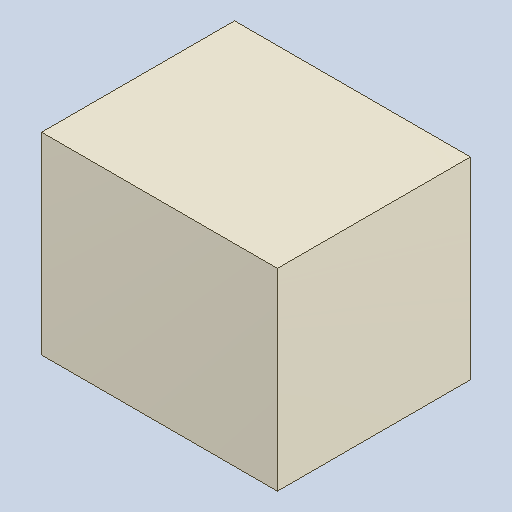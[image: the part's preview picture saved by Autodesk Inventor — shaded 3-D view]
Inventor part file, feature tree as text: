
AUTODESK INVENTOR PART (.ipt)
format: ipt  version: 2023.4 (Build 274418000, 418)  size: 81,920 bytes
history: native  units: mm
features: extrude x1
ambient origin geometry x8: Origin, YZ Plane, XZ Plane, XY Plane, X Axis, Y Axis, Z Axis, Center Point
bodies: Solid1 (feature_tree)
feature tree (1):
  extrude  "Extruded_17"  [1 undecoded]
note: 1 required parameter value undecoded (feature->parameter linkage not recoverable at this tier; creation-order binding heuristic only, values carry confidence <= 0.55)
